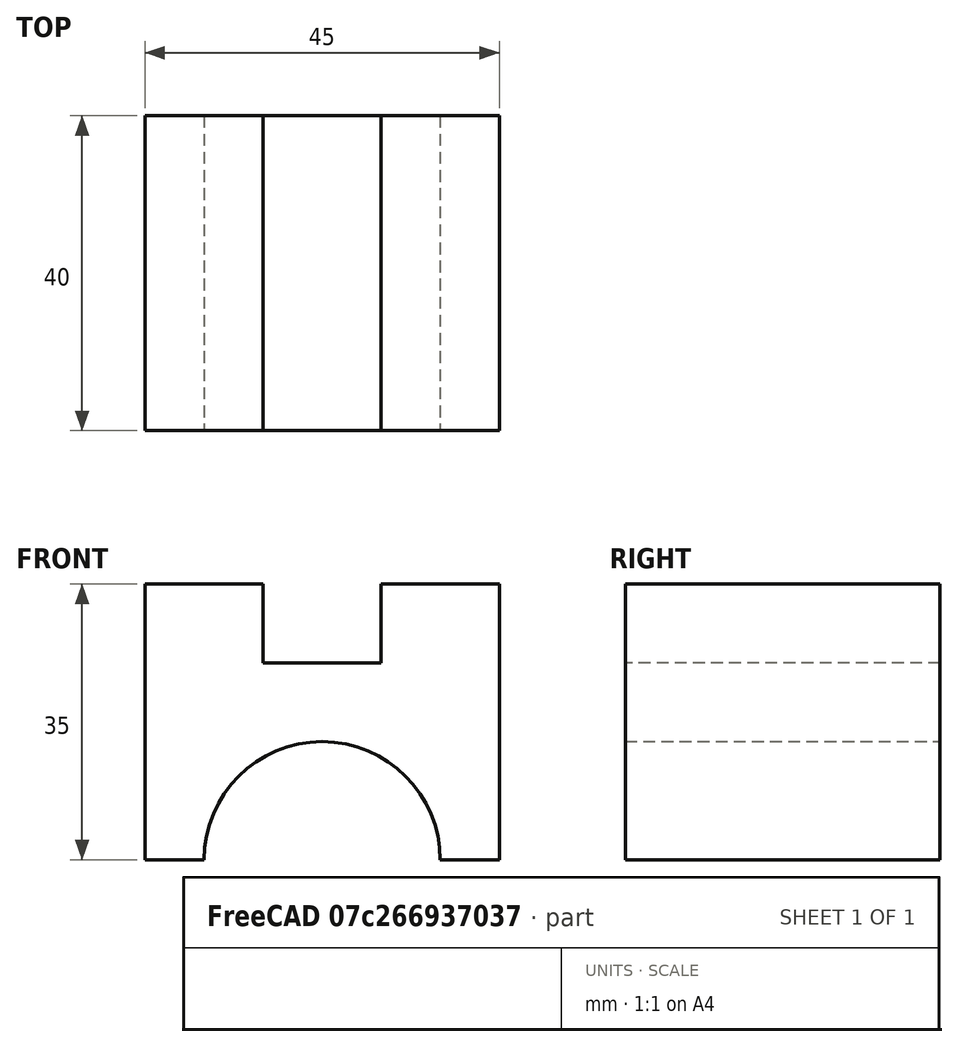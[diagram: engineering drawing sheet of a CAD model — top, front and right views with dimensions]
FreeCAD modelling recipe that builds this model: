
FCSTD DOCUMENT  (FreeCAD 0.20R29410 (Git))
Label: ISO-PRAC2
License: All rights reserved
LicenseURL: http://en.wikipedia.org/wiki/All_rights_reserved
objects: Sketcher::SketchObject×1, PartDesign::Pad×1, PartDesign::Body×1
note: 4 computed .brp shape members not serialized (recipe doc carries the construction recipe); baked Part::Feature solids carry a one-line shape summary decoded from their .brp

FEATURE [Sketcher::SketchObject] Sketch
  FullyConstrained = true
  MapMode = 5
  Placement = pos=(0,0,0) rot=(1,0,0;1.5708rad)
  Support = -> [XZ_Plane]
  sketch-geometry (10):
    g0: LineSegment StartX=-22.5 StartY=-4.8e-15 StartZ=0 EndX=-22.5 EndY=35 EndZ=0
    g1: LineSegment StartX=-22.5 StartY=35 StartZ=0 EndX=-7.5 EndY=35 EndZ=0
    g2: LineSegment StartX=-7.5 StartY=35 StartZ=0 EndX=-7.5 EndY=25 EndZ=0
    g3: LineSegment StartX=-7.5 StartY=25 StartZ=0 EndX=7.5 EndY=25 EndZ=0
    g4: LineSegment StartX=7.5 StartY=25 StartZ=0 EndX=7.5 EndY=35 EndZ=0
    g5: LineSegment StartX=7.5 StartY=35 StartZ=0 EndX=22.5 EndY=35 EndZ=0
    g6: LineSegment StartX=22.5 StartY=35 StartZ=0 EndX=22.5 EndY=0 EndZ=0
    g7: LineSegment StartX=22.5 StartY=0 StartZ=0 EndX=15 EndY=0 EndZ=0
    g8: ArcOfCircle CenterX=0 CenterY=0 CenterZ=0 NormalX=0 NormalY=0 NormalZ=1 AngleXU=0 Radius=15 StartAngle=0 EndAngle=3.14159
    g9: LineSegment StartX=-15 StartY=-4.8e-15 StartZ=0 EndX=-22.5 EndY=-4.8e-15 EndZ=0
  constraints (29):
    c: Coincident(g0,g1)
    c: Coincident(g1,g2)
    c: Coincident(g2,g3)
    c: Coincident(g3,g4)
    c: Coincident(g4,g5)
    c: Horizontal(g5)
    c: Coincident(g5,g6)
    c: Coincident(g6,g7)
    c: Horizontal(g7)
    c: Perpendicular(g7,g8) = 4.71239
    c: Coincident(g8,g9)
    c: Coincident(g9,g0)
    c: Vertical(g6)
    c: Vertical(g0)
    c: Vertical(g2)
    c: Vertical(g4)
    c: Horizontal(g1)
    c: Horizontal(g3)
    c: Horizontal(g9)
    c: Equal(g0,g6)
    c: Equal(g3,g1)
    c: Equal(g1,g5)
    c: Equal(g2,g4)
    c: DistanceX(g1,g1) = 15
    c: DistanceY(g2,g2) = 10
    c: DistanceY(g0,g0) = 35
    c: Radius(g8) = 15
    c: Equal(g9,g7)
    c: Coincident(g8,g-1)
FEATURE [PartDesign::Pad] Pad
  Direction = (0,-1,2e-16)
  Length = 40
  Length2 = 10
  Placement = pos=(0,0,0) rot=(1,0,0;1.5708rad)
  Profile = -> Sketch
  ReferenceAxis = -> Sketch [N_Axis]
  Refine = true
  Type = 0
FEATURE [PartDesign::Body] Body
  Group = -> [Sketch,Pad]
  Origin = -> Origin
  Tip = -> Pad
